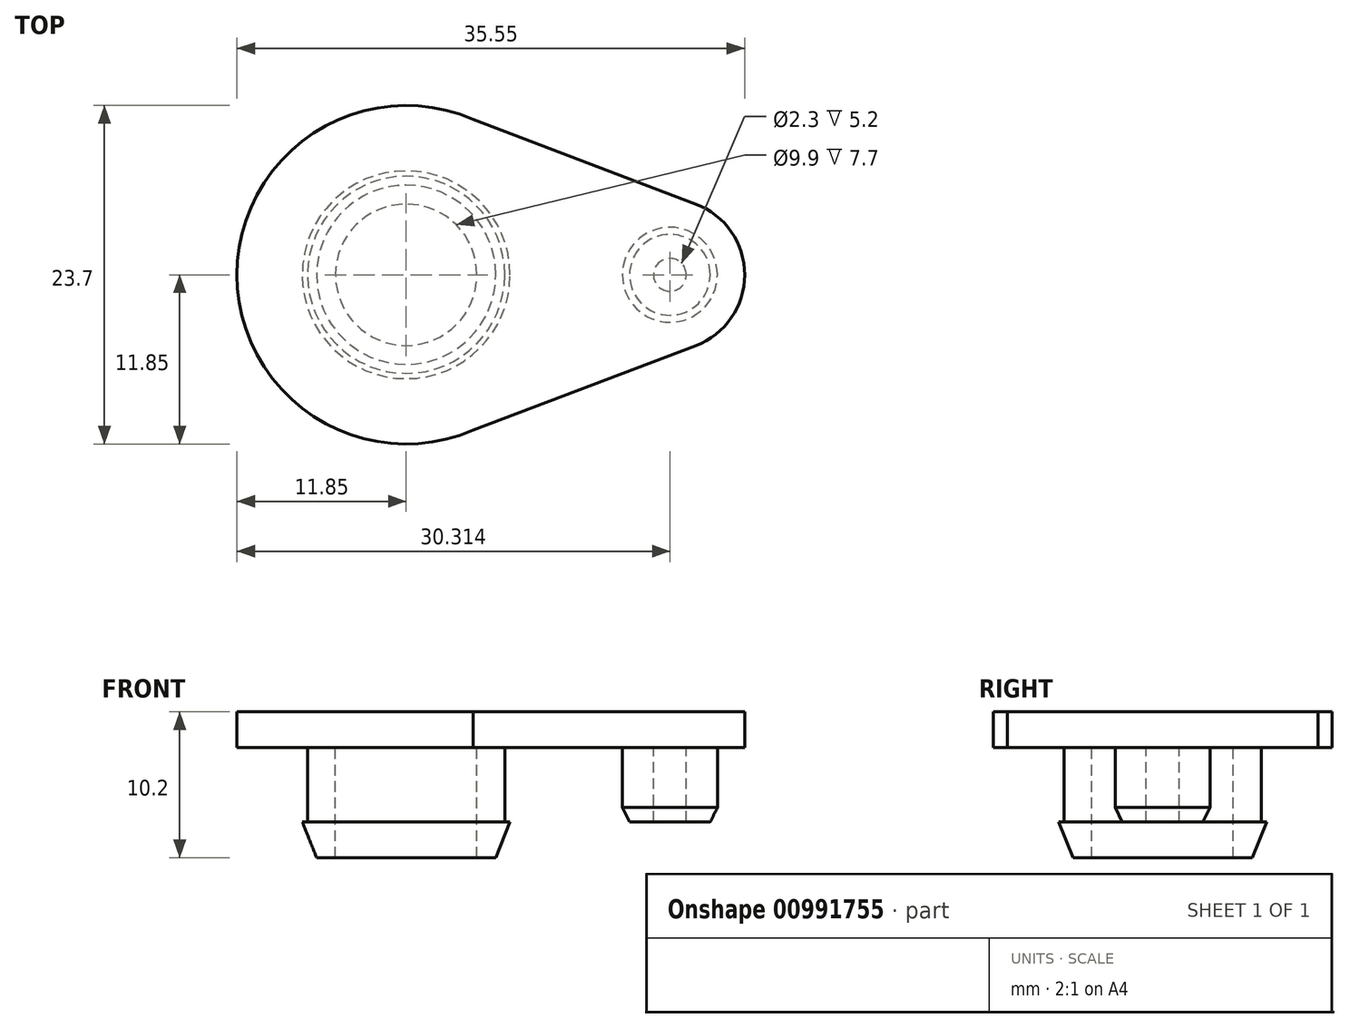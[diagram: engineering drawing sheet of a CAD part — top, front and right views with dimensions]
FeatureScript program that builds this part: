
annotation { "Feature Type Name" : "Feature", "Feature Type Description" : "" }
export const myFeature = defineFeature(function(context is Context, id is Id, definition is map)
    precondition{}
    {
        {
            var Q0;
            Q0=qCreatedBy(makeId("Top.planeOp"),FACE);
            var sketch = newSketch(context, id + "F0", { "sketchPlane" : qUnion([Q0])});
            skCircle(sketch, "E0", {"center": v(0, 0) * mm, "radius": 11.85 * mm});
            skCircle(sketch, "E1", {"center": v(18.4, 0) * mm, "radius": 5.3 * mm});
            skLineSegment(sketch, "E2", {"start": v(3.73, 11.25) * mm, "end": v(20.28, 4.95) * mm});
            skLineSegment(sketch, "E3.MirrorCS", {"start": v(3.73, -11.25) * mm, "end": v(20.28, -4.95) * mm});
            skSolve(sketch);
        }
        {
            var Q0;
            Q0 = qSketchRegion(id + "F0", true);
            extrude(context, id + "F1", {"entities" : qUnion([Q0]), "depth" : 2.5 * mm, "offsetDistance" : 25 * mm});
        }
        {
            var Q0;
            Q0=qCreatedBy(makeId("Top.planeOp"),FACE);
            var sketch = newSketch(context, id + "F2", { "sketchPlane" : qUnion([Q0])});
            skCircle(sketch, "E4", {"center": v(0, 0) * mm, "radius": 6.9 * mm});
            skCircle(sketch, "E5", {"center": v(0, 0) * mm, "radius": 4.95 * mm});
            skCircle(sketch, "E6", {"center": v(18.46, 0) * mm, "radius": 3.33 * mm});
            skCircle(sketch, "E7", {"center": v(18.46, 0) * mm, "radius": 1.15 * mm});
            skSolve(sketch);
        }
        {
            var Q0;
            Q0 = qSketchRegion(id + "F2", true);
            extrude(context, id + "F3", {"entities" : qUnion([Q0]), "operationType" : NewBodyOperationType.ADD, "oppositeDirection" : true, "depth" : 5.2 * mm, "offsetDistance" : 25 * mm});
        }
        {
            var Q0;
            Q0=makeQuery(id+"F3.opExtrude","CAP_FACE",FACE,{"disambiguationData":[OSD([sQuery(id+"F2.wireOp",EDGE,"E4"),sQuery(id+"F2.wireOp",EDGE,"E5")])],"isStart":false});
            var sketch = newSketch(context, id + "F4", { "sketchPlane" : qUnion([Q0])});
            skCircle(sketch, "E8", {"center": v(0, 0) * mm, "radius": 4.95 * mm});
            skCircle(sketch, "E9", {"center": v(0, 0) * mm, "radius": 7.28 * mm});
            skSolve(sketch);
        }
        {
            var Q0;
            Q0 = qSketchRegion(id + "F4", true);
            extrude(context, id + "F5", {"entities" : qUnion([Q0]), "operationType" : NewBodyOperationType.ADD, "depth" : 2.5 * mm, "offsetDistance" : 25 * mm});
        }
        {
            var Q0;
            Q0=makeQuery(id+"F5.opExtrude","CAP_EDGE",EDGE,{"disambiguationData":[OSD([sQuery(id+"F4.wireOp",EDGE,"E9")])],"isStart":false});
            chamfer(context, id + "F6", {"entities" : qUnion([Q0]), "chamferType" : ChamferType.TWO_OFFSETS, "width1" : 1 * mm, "oppositeDirection" : false, "width2" : 2.5 * mm, "tangentPropagation" : true});
        }
        {
            var Q0;
            Q0=makeQuery(id+"F3.opExtrude","CAP_EDGE",EDGE,{"disambiguationData":[OSD([sQuery(id+"F2.wireOp",EDGE,"E6")])],"isStart":false});
            chamfer(context, id + "F7", {"entities" : qUnion([Q0]), "chamferType" : ChamferType.TWO_OFFSETS, "width1" : 0.5 * mm, "oppositeDirection" : true, "width2" : 1 * mm, "tangentPropagation" : true});
        }
    });
